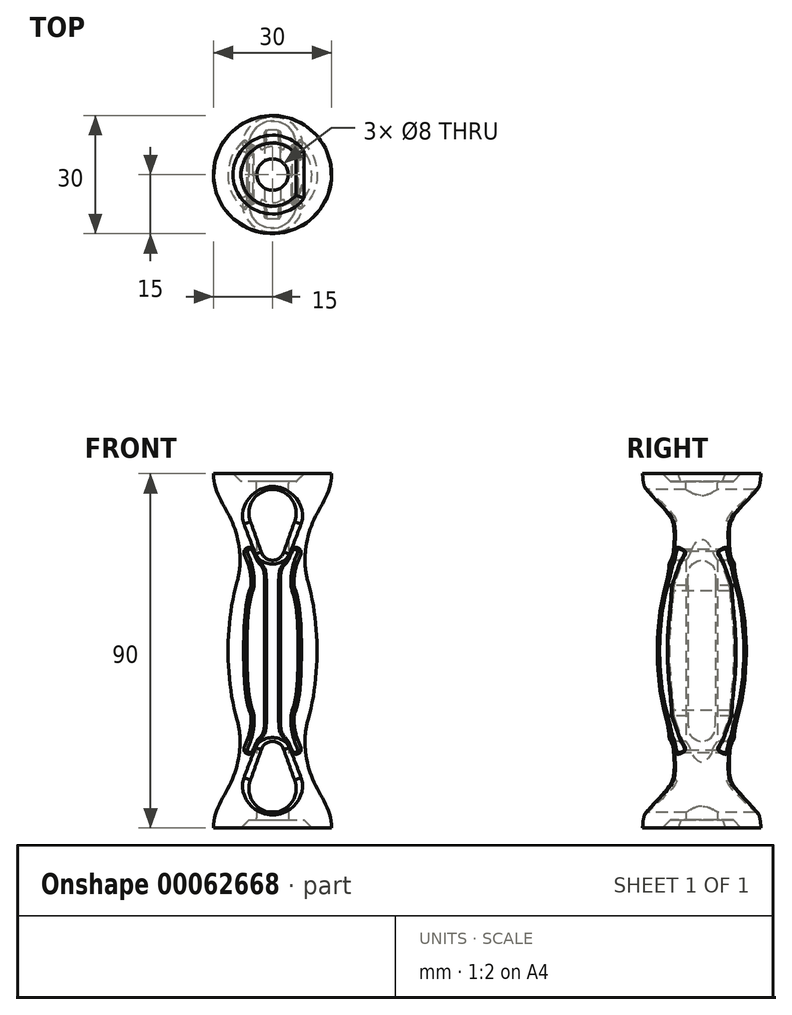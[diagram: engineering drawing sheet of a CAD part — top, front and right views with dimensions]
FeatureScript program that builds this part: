
annotation { "Feature Type Name" : "Feature", "Feature Type Description" : "" }
export const myFeature = defineFeature(function(context is Context, id is Id, definition is map)
    precondition{}
    {
        {
            var Q0;
            Q0=qCreatedBy(makeId("Front.planeOp"),FACE);
            var sketch = newSketch(context, id + "F0", { "sketchPlane" : qUnion([Q0])});
            skLineSegment(sketch, "E0", {"start": v(0, 0) * mm, "end": v(0, 45) * mm});
            skLineSegment(sketch, "E1", {"start": v(0, 45) * mm, "end": v(-15, 45) * mm});
            skLineSegment(sketch, "E2", {"start": v(0, 0) * mm, "end": v(-8, 0) * mm});
            skFitSpline(sketch, "E3", {"points": [v(-15, 45) * mm, v(-9.89, 31.85) * mm, v(-7.97, 5.04) * mm], "startDerivative": vector(-0.53, -36.4) * mm, "endDerivative": vector(-0.2, -58.1) * mm});
            skLineSegment(sketch, "E4.MirrorCS", {"start": v(0, -45) * mm, "end": v(-15, -45) * mm});
            skLineSegment(sketch, "E5.MirrorCS", {"start": v(0, 0) * mm, "end": v(0, -45) * mm});
            skFitSpline(sketch, "E6.MirrorCS", {"points": [v(-15, -45) * mm, v(-9.89, -31.85) * mm, v(-7.97, -5.04) * mm], "startDerivative": vector(-0.53, 36.4) * mm, "endDerivative": vector(-0.2, 58.1) * mm});
            skEllipticalArc(sketch, "E7", {});
            skPoint(sketch, "E8.MirrorCS.start.orphan", {"position": v(-8, 0) * mm});
            skPoint(sketch, "E9.visualSharp", {"position": v(-8, 20.72) * mm});
            skArc(sketch, "E9.filletArc", {"start": v(-9, 17.6) * mm, "mid": v(-8.3, 21.6) * mm, "end": v(-8.41, 25.67) * mm});
            skPoint(sketch, "E10.visualSharp", {"position": v(-8, -20.72) * mm});
            skArc(sketch, "E10.filletArc", {"start": v(-8.41, -25.67) * mm, "mid": v(-8.3, -21.6) * mm, "end": v(-9, -17.6) * mm});
            const initialGuessF0  = {"E7": [0.0066548618488013744, 0, 0, 1, 0.03582403436303139, 0.017969114314154242, 1.0572183333888945, 2.0843743202008995]};
            skSetInitialGuess(sketch, initialGuessF0);
            skSolve(sketch);
        }
        {
            var Q0;
            Q0=qSketchRegion(id+"F0",true);
            var Q1;
            Q1=sQuery(id+"F0.wireOp",EDGE,"E5.MirrorCS");
            revolve(context, id + "F1", {"entities" : qUnion([Q0]), "axis" : qUnion([Q1]), "revolveType" : RevolveType.FULL});
        }
        {
            var Q0;
            Q0=makeQuery(id+"F1.opRevolve","SWEPT_FACE",FACE,{"disambiguationData":[OSD([sQuery(id+"F0.wireOp",EDGE,"E4.MirrorCS")])]});
            var sketch = newSketch(context, id + "F2", { "sketchPlane" : qUnion([Q0])});
            skCircle(sketch, "E11", {"center": v(0, 0) * mm, "radius": 4 * mm});
            skSolve(sketch);
        }
        {
            var Q0;
            Q0=qSketchRegion(id+"F2",true);
            extrude(context, id + "F3", {"entities" : qUnion([Q0]), "operationType" : NewBodyOperationType.REMOVE, "oppositeDirection" : true, "depth" : 10 * mm});
        }
        {
            var Q0;
            Q0=qCreatedBy(makeId("Front.planeOp"),FACE);
            var sketch = newSketch(context, id + "F4", { "sketchPlane" : qUnion([Q0])});
            skLineSegment(sketch, "E12", {"start": v(0, 0) * mm, "end": v(0, 35) * mm});
            skArc(sketch, "E13", {"start": v(5.66, 33) * mm, "mid": v(0, 41) * mm, "end": v(-5.66, 33) * mm});
            skArc(sketch, "E14", {"start": v(-2.83, 25) * mm, "mid": v(0, 23) * mm, "end": v(2.83, 25) * mm});
            skLineSegment(sketch, "E15", {"start": v(5.66, 33) * mm, "end": v(2.83, 25) * mm});
            skLineSegment(sketch, "E16", {"start": v(-2.83, 25) * mm, "end": v(-5.66, 33) * mm});
            skLineSegment(sketch, "E17.MirrorCS", {"start": v(5.66, -33) * mm, "end": v(2.83, -25) * mm});
            skLineSegment(sketch, "E18.MirrorCS", {"start": v(0, 0) * mm, "end": v(0, -35) * mm});
            skLineSegment(sketch, "E19.MirrorCS", {"start": v(-2.83, -25) * mm, "end": v(-5.66, -33) * mm});
            skArc(sketch, "E20.MirrorCS", {"start": v(5.66, -33) * mm, "mid": v(0, -41) * mm, "end": v(-5.66, -33) * mm});
            skArc(sketch, "E21.MirrorCS", {"start": v(-2.83, -25) * mm, "mid": v(0, -23) * mm, "end": v(2.83, -25) * mm});
            skLineSegment(sketch, "E22", {"start": v(2, 16.6) * mm, "end": v(2, -16.6) * mm});
            skPoint(sketch, "E22.startSnap0", {"position": v(0, 17.5) * mm});
            skPoint(sketch, "E22.endSnap0", {"position": v(0, -17.5) * mm});
            skFitSpline(sketch, "E23", {"points": [v(2, 18) * mm, v(6.5, 0) * mm, v(2, -18) * mm], "startDerivative": vector(24, 0) * mm, "endDerivative": vector(-24, 0) * mm});
            skLineSegment(sketch, "E24.MirrorCS", {"start": v(-2, -16.6) * mm, "end": v(-2, -16.6) * mm});
            skPoint(sketch, "E25.MirrorP", {"position": v(-2, 18) * mm});
            skLineSegment(sketch, "E26.MirrorCS", {"start": v(-2, 16.6) * mm, "end": v(-2, -16.6) * mm});
            skFitSpline(sketch, "E27.MirrorCS", {"points": [v(-2, 18) * mm, v(-6.5, 0) * mm, v(-2, -18) * mm], "startDerivative": vector(-24, 0) * mm, "endDerivative": vector(24, 0) * mm});
            skFitSpline(sketch, "E28", {"points": [v(6.31, 25.3) * mm, v(6.31, 24.87) * mm, v(5.43, 22.53) * mm, v(4.64, 17.15) * mm, v(5.01, 15.16) * mm], "startDerivative": vector(0.28, -3.35) * mm, "endDerivative": vector(2.24, -7.03) * mm});
            skFitSpline(sketch, "E29", {"points": [v(6.31, 25.3) * mm, v(6.08, 25.65) * mm, v(5.45, 25.79) * mm, v(3.9, 22.88) * mm, v(2.45, 20.92) * mm, v(2, 16.6) * mm], "startDerivative": vector(-1.1, 4.8) * mm, "endDerivative": vector(0.4, -12.77) * mm});
            skPoint(sketch, "E30.filletArc.start.orphan", {"position": v(3.67, 17.34) * mm});
            skFitSpline(sketch, "E31.MirrorCS", {"points": [v(-6.31, 25.3) * mm, v(-6.31, 24.87) * mm, v(-5.43, 22.53) * mm, v(-4.64, 17.15) * mm, v(-5.01, 15.16) * mm], "startDerivative": vector(-0.28, -3.35) * mm, "endDerivative": vector(-2.24, -7.03) * mm});
            skFitSpline(sketch, "E32.MirrorCS", {"points": [v(-6.31, 25.3) * mm, v(-6.08, 25.65) * mm, v(-5.45, 25.79) * mm, v(-3.9, 22.88) * mm, v(-2.45, 20.92) * mm, v(-2, 16.6) * mm], "startDerivative": vector(1.1, 4.8) * mm, "endDerivative": vector(-0.4, -12.77) * mm});
            skPoint(sketch, "E33.MirrorCS.start.orphan", {"position": v(-3.67, 17.34) * mm});
            skLineSegment(sketch, "E34", {"start": v(0, 0) * mm, "end": v(-2, 0) * mm});
            skPoint(sketch, "E34.endSnap0", {"position": v(-2, 0) * mm});
            skFitSpline(sketch, "E35.MirrorCS", {"points": [v(6.31, -25.3) * mm, v(6.31, -24.87) * mm, v(5.43, -22.53) * mm, v(4.64, -17.15) * mm, v(5.01, -15.16) * mm], "startDerivative": vector(0.28, 3.35) * mm, "endDerivative": vector(2.24, 7.03) * mm});
            skFitSpline(sketch, "E36.MirrorCS", {"points": [v(6.31, -25.3) * mm, v(6.08, -25.65) * mm, v(5.45, -25.79) * mm, v(3.9, -22.88) * mm, v(2.45, -20.92) * mm, v(2, -16.6) * mm], "startDerivative": vector(-1.1, -4.8) * mm, "endDerivative": vector(0.4, 12.77) * mm});
            skFitSpline(sketch, "E37.MirrorCS", {"points": [v(-6.31, -25.3) * mm, v(-6.08, -25.65) * mm, v(-5.45, -25.79) * mm, v(-3.9, -22.88) * mm, v(-2.45, -20.92) * mm, v(-2, -16.6) * mm], "startDerivative": vector(1.1, -4.8) * mm, "endDerivative": vector(-0.4, 12.77) * mm});
            skFitSpline(sketch, "E38.MirrorCS", {"points": [v(-6.31, -25.3) * mm, v(-6.31, -24.87) * mm, v(-5.43, -22.53) * mm, v(-4.64, -17.15) * mm, v(-5.01, -15.16) * mm], "startDerivative": vector(-0.28, 3.35) * mm, "endDerivative": vector(-2.24, 7.03) * mm});
            skPoint(sketch, "E39.orphan", {"position": v(-3.67, -17.34) * mm});
            skPoint(sketch, "E40.filletArc.end.orphan", {"position": v(3.67, -17.34) * mm});
            skSolve(sketch);
        }
        {
            var Q0;
            Q0=qSketchRegion(id+"F4",true);
            extrude(context, id + "F5", {"entities" : qUnion([Q0]), "operationType" : NewBodyOperationType.REMOVE, "endBound" : BoundingType.THROUGH_ALL, "oppositeDirection" : true, "depth" : 25 * mm, "hasSecondDirection" : true, "secondDirectionOppositeDirection" : false, "secondDirectionDepth" : 25 * mm});
        }
        {
            var Q0;
            Q0=makeQuery(id+"F1.opRevolve","SWEPT_FACE",FACE,{"disambiguationData":[OSD([sQuery(id+"F0.wireOp",EDGE,"E1")])]});
            var sketch = newSketch(context, id + "F6", { "sketchPlane" : qUnion([Q0])});
            skCircle(sketch, "E41", {"center": v(0, 0) * mm, "radius": 4 * mm});
            skSolve(sketch);
        }
        {
            var Q0;
            Q0=qSketchRegion(id+"F6",true);
            extrude(context, id + "F7", {"entities" : qUnion([Q0]), "operationType" : NewBodyOperationType.REMOVE, "oppositeDirection" : true, "depth" : 10 * mm});
        }
        {
            var Q0;
            Q0=makeQuery(id+"F1.opRevolve","SWEPT_FACE",FACE,{"disambiguationData":[OSD([sQuery(id+"F0.wireOp",EDGE,"E4.MirrorCS")])]});
            var sketch = newSketch(context, id + "F8", { "sketchPlane" : qUnion([Q0])});
            skArc(sketch, "E42", {"start": v(-8, -6) * mm, "mid": v(10, 0) * mm, "end": v(-8, 6) * mm});
            skLineSegment(sketch, "E43", {"start": v(-8, -6) * mm, "end": v(-8, 6) * mm});
            skSolve(sketch);
        }
        {
            var Q0;
            Q0=qSketchRegion(id+"F8",true);
            extrude(context, id + "F9", {"entities" : qUnion([Q0]), "operationType" : NewBodyOperationType.REMOVE, "oppositeDirection" : true, "depth" : 2 * mm, "hasDraft" : true, "draftAngle" : 45 * degree, "draftPullDirection" : true});
        }
        {
            var Q0;
            Q0=makeQuery(id+"F1.opRevolve","SWEPT_FACE",FACE,{"disambiguationData":[OSD([sQuery(id+"F0.wireOp",EDGE,"E1")])]});
            var sketch = newSketch(context, id + "F10", { "sketchPlane" : qUnion([Q0])});
            skArc(sketch, "E44", {"start": v(8, 6) * mm, "mid": v(-10, 0) * mm, "end": v(8, -6) * mm});
            skLineSegment(sketch, "E45", {"start": v(8, 6) * mm, "end": v(8, -6) * mm});
            skSolve(sketch);
        }
        {
            var Q0;
            Q0=qSketchRegion(id+"F10",true);
            extrude(context, id + "F11", {"entities" : qUnion([Q0]), "operationType" : NewBodyOperationType.REMOVE, "oppositeDirection" : true, "depth" : 2 * mm, "hasDraft" : true, "draftAngle" : 45 * degree, "draftPullDirection" : true});
        }
        {
            var Q0;
            Q0=makeQuery(id+"F9.boolean.opBoolean","COPY",EDGE,{"derivedFrom":makeQuery(id+"F9.opExtrude","CAP_EDGE",EDGE,{"disambiguationData":[OSD([sQuery(id+"F8.wireOp",EDGE,"E42")])],"isStart":true})});
            var Q1;
            Q1=makeQuery(id+"F9.boolean.opBoolean","INTERSECT",EDGE,{"derivedFrom":[makeQuery(id+"F3.boolean.opBoolean","COPY",FACE,{"derivedFrom":makeQuery(id+"F3.opExtrude","SWEPT_FACE",FACE,{"disambiguationData":[OSD([sQuery(id+"F2.wireOp",EDGE,"E11")])]})}),makeQuery(id+"F9.opExtrude","CAP_FACE",FACE,{"disambiguationData":[OSD([sQuery(id+"F8.wireOp",EDGE,"E42")])],"isStart":false})]});
            var Q2;
            Q2=makeQuery(id+"F11.boolean.opBoolean","COPY",EDGE,{"derivedFrom":makeQuery(id+"F11.opExtrude","CAP_EDGE",EDGE,{"disambiguationData":[OSD([sQuery(id+"F10.wireOp",EDGE,"E44")])],"isStart":true})});
            var Q3;
            Q3=makeQuery(id+"F11.boolean.opBoolean","INTERSECT",EDGE,{"derivedFrom":[makeQuery(id+"F7.boolean.opBoolean","COPY",FACE,{"derivedFrom":makeQuery(id+"F7.opExtrude","SWEPT_FACE",FACE,{"disambiguationData":[OSD([sQuery(id+"F6.wireOp",EDGE,"E41")])]})}),makeQuery(id+"F11.opExtrude","CAP_FACE",FACE,{"disambiguationData":[OSD([sQuery(id+"F10.wireOp",EDGE,"E44")])],"isStart":false})]});
            var Q4;
            Q4=makeQuery(id+"F11.boolean.opBoolean","COPY",EDGE,{"derivedFrom":makeQuery(id+"F11.opExtrude","CAP_EDGE",EDGE,{"disambiguationData":[OSD([sQuery(id+"F10.wireOp",EDGE,"E45")])],"isStart":true})});
            var Q5;
            Q5=makeQuery(id+"F9.boolean.opBoolean","COPY",EDGE,{"derivedFrom":makeQuery(id+"F9.opExtrude","CAP_EDGE",EDGE,{"disambiguationData":[OSD([sQuery(id+"F8.wireOp",EDGE,"E43")])],"isStart":true})});
            fillet(context, id + "F12", {"entities" : qUnion([Q0, Q1, Q2, Q3, Q4, Q5]), "radius" : .5 * mm, "tangentPropagation" : true, "allowEdgeOverflow" : false});
        }
        {
            var Q0;
            Q0=makeQuery(id+"F9.boolean.opBoolean","COPY",FACE,{"derivedFrom":makeQuery(id+"F9.opExtrude","CAP_FACE",FACE,{"disambiguationData":[OSD([sQuery(id+"F8.wireOp",EDGE,"E42")])],"isStart":false})});
            var sketch = newSketch(context, id + "F13", { "sketchPlane" : qUnion([Q0])});
            skCircle(sketch, "E46", {"center": v(0, 0) * mm, "radius": 4 * mm});
            skSolve(sketch);
        }
        {
            var Q0;
            Q0=qSketchRegion(id+"F13",true);
            extrude(context, id + "F14", {"entities" : qUnion([Q0]), "operationType" : NewBodyOperationType.REMOVE, "endBound" : BoundingType.THROUGH_ALL, "oppositeDirection" : true, "depth" : 25 * mm});
        }
        {
            var Q0;
            Q0=makeQuery(id+"F5.boolean.opBoolean","INTERSECT",EDGE,{"disambiguationData":[OD(0.0)],"derivedFrom":[makeQuery(id+"F1.opRevolve","SWEPT_FACE",FACE,{"disambiguationData":[OSD([sQuery(id+"F0.wireOp",EDGE,"E6.MirrorCS")])]}),makeQuery(id+"F5.opExtrude","SWEPT_FACE",FACE,{"disambiguationData":[OSD([sQuery(id+"F4.wireOp",EDGE,"E20.MirrorCS")])]})]});
            var Q1;
            Q1=makeQuery(id+"F5.boolean.opBoolean","INTERSECT",EDGE,{"disambiguationData":[OD(0.0)],"derivedFrom":[makeQuery(id+"F1.opRevolve","SWEPT_FACE",FACE,{"disambiguationData":[OSD([sQuery(id+"F0.wireOp",EDGE,"E6.MirrorCS")])]}),makeQuery(id+"F5.opExtrude","SWEPT_FACE",FACE,{"disambiguationData":[OSD([sQuery(id+"F4.wireOp",EDGE,"E19.MirrorCS")])]})]});
            var Q2;
            Q2=makeQuery(id+"F5.boolean.opBoolean","INTERSECT",EDGE,{"disambiguationData":[OD(1.0)],"derivedFrom":[makeQuery(id+"F1.opRevolve","SWEPT_FACE",FACE,{"disambiguationData":[OSD([sQuery(id+"F0.wireOp",EDGE,"E6.MirrorCS")])]}),makeQuery(id+"F5.opExtrude","SWEPT_FACE",FACE,{"disambiguationData":[OSD([sQuery(id+"F4.wireOp",EDGE,"E20.MirrorCS")])]})]});
            var Q3;
            Q3=makeQuery(id+"F5.boolean.opBoolean","INTERSECT",EDGE,{"disambiguationData":[OD(0.0)],"derivedFrom":[makeQuery(id+"F1.opRevolve","SWEPT_FACE",FACE,{"disambiguationData":[OSD([sQuery(id+"F0.wireOp",EDGE,"E6.MirrorCS")])]}),makeQuery(id+"F5.opExtrude","SWEPT_FACE",FACE,{"disambiguationData":[OSD([sQuery(id+"F4.wireOp",EDGE,"E17.MirrorCS")])]})]});
            var Q4;
            Q4=makeQuery(id+"F5.boolean.opBoolean","INTERSECT",EDGE,{"disambiguationData":[OD(0.0)],"derivedFrom":[makeQuery(id+"F1.opRevolve","SWEPT_FACE",FACE,{"disambiguationData":[OSD([sQuery(id+"F0.wireOp",EDGE,"E10.filletArc")])]}),makeQuery(id+"F5.opExtrude","SWEPT_FACE",FACE,{"disambiguationData":[OSD([sQuery(id+"F4.wireOp",EDGE,"E21.MirrorCS")])]})]});
            var Q5;
            Q5=makeQuery(id+"F5.boolean.opBoolean","INTERSECT",EDGE,{"disambiguationData":[OD(0.0)],"derivedFrom":[makeQuery(id+"F1.opRevolve","SWEPT_FACE",FACE,{"disambiguationData":[OSD([sQuery(id+"F0.wireOp",EDGE,"E10.filletArc")])]}),makeQuery(id+"F5.opExtrude","SWEPT_FACE",FACE,{"disambiguationData":[OSD([sQuery(id+"F4.wireOp",EDGE,"E19.MirrorCS")])]})]});
            var Q6;
            Q6=makeQuery(id+"F5.boolean.opBoolean","INTERSECT",EDGE,{"disambiguationData":[OD(0.0)],"derivedFrom":[makeQuery(id+"F1.opRevolve","SWEPT_FACE",FACE,{"disambiguationData":[OSD([sQuery(id+"F0.wireOp",EDGE,"E10.filletArc")])]}),makeQuery(id+"F5.opExtrude","SWEPT_FACE",FACE,{"disambiguationData":[OSD([sQuery(id+"F4.wireOp",EDGE,"E17.MirrorCS")])]})]});
            var Q7;
            Q7=makeQuery(id+"F5.boolean.opBoolean","INTERSECT",EDGE,{"disambiguationData":[OD(1.0)],"derivedFrom":[makeQuery(id+"F1.opRevolve","SWEPT_FACE",FACE,{"disambiguationData":[OSD([sQuery(id+"F0.wireOp",EDGE,"E6.MirrorCS")])]}),makeQuery(id+"F5.opExtrude","SWEPT_FACE",FACE,{"disambiguationData":[OSD([sQuery(id+"F4.wireOp",EDGE,"E17.MirrorCS")])]})]});
            var Q8;
            Q8=makeQuery(id+"F5.boolean.opBoolean","INTERSECT",EDGE,{"disambiguationData":[OD(1.0)],"derivedFrom":[makeQuery(id+"F1.opRevolve","SWEPT_FACE",FACE,{"disambiguationData":[OSD([sQuery(id+"F0.wireOp",EDGE,"E6.MirrorCS")])]}),makeQuery(id+"F5.opExtrude","SWEPT_FACE",FACE,{"disambiguationData":[OSD([sQuery(id+"F4.wireOp",EDGE,"E19.MirrorCS")])]})]});
            var Q9;
            Q9=makeQuery(id+"F5.boolean.opBoolean","INTERSECT",EDGE,{"disambiguationData":[OD(1.0)],"derivedFrom":[makeQuery(id+"F1.opRevolve","SWEPT_FACE",FACE,{"disambiguationData":[OSD([sQuery(id+"F0.wireOp",EDGE,"E10.filletArc")])]}),makeQuery(id+"F5.opExtrude","SWEPT_FACE",FACE,{"disambiguationData":[OSD([sQuery(id+"F4.wireOp",EDGE,"E21.MirrorCS")])]})]});
            var Q10;
            Q10=makeQuery(id+"F5.boolean.opBoolean","INTERSECT",EDGE,{"disambiguationData":[OD(1.0)],"derivedFrom":[makeQuery(id+"F1.opRevolve","SWEPT_FACE",FACE,{"disambiguationData":[OSD([sQuery(id+"F0.wireOp",EDGE,"E10.filletArc")])]}),makeQuery(id+"F5.opExtrude","SWEPT_FACE",FACE,{"disambiguationData":[OSD([sQuery(id+"F4.wireOp",EDGE,"E19.MirrorCS")])]})]});
            var Q11;
            Q11=makeQuery(id+"F5.boolean.opBoolean","INTERSECT",EDGE,{"disambiguationData":[OD(1.0)],"derivedFrom":[makeQuery(id+"F1.opRevolve","SWEPT_FACE",FACE,{"disambiguationData":[OSD([sQuery(id+"F0.wireOp",EDGE,"E10.filletArc")])]}),makeQuery(id+"F5.opExtrude","SWEPT_FACE",FACE,{"disambiguationData":[OSD([sQuery(id+"F4.wireOp",EDGE,"E17.MirrorCS")])]})]});
            var Q12;
            Q12=makeQuery(id+"F5.boolean.opBoolean","INTERSECT",EDGE,{"disambiguationData":[OD(0.0)],"derivedFrom":[makeQuery(id+"F1.opRevolve","SWEPT_FACE",FACE,{"disambiguationData":[OSD([sQuery(id+"F0.wireOp",EDGE,"E9.filletArc")])]}),makeQuery(id+"F5.opExtrude","SWEPT_FACE",FACE,{"disambiguationData":[OSD([sQuery(id+"F4.wireOp",EDGE,"E14")])]})]});
            var Q13;
            Q13=makeQuery(id+"F5.boolean.opBoolean","INTERSECT",EDGE,{"disambiguationData":[OD(0.0)],"derivedFrom":[makeQuery(id+"F1.opRevolve","SWEPT_FACE",FACE,{"disambiguationData":[OSD([sQuery(id+"F0.wireOp",EDGE,"E9.filletArc")])]}),makeQuery(id+"F5.opExtrude","SWEPT_FACE",FACE,{"disambiguationData":[OSD([sQuery(id+"F4.wireOp",EDGE,"E16")])]})]});
            var Q14;
            Q14=makeQuery(id+"F5.boolean.opBoolean","INTERSECT",EDGE,{"disambiguationData":[OD(0.0)],"derivedFrom":[makeQuery(id+"F1.opRevolve","SWEPT_FACE",FACE,{"disambiguationData":[OSD([sQuery(id+"F0.wireOp",EDGE,"E9.filletArc")])]}),makeQuery(id+"F5.opExtrude","SWEPT_FACE",FACE,{"disambiguationData":[OSD([sQuery(id+"F4.wireOp",EDGE,"E15")])]})]});
            var Q15;
            Q15=makeQuery(id+"F5.boolean.opBoolean","INTERSECT",EDGE,{"disambiguationData":[OD(0.0)],"derivedFrom":[makeQuery(id+"F1.opRevolve","SWEPT_FACE",FACE,{"disambiguationData":[OSD([sQuery(id+"F0.wireOp",EDGE,"E3")])]}),makeQuery(id+"F5.opExtrude","SWEPT_FACE",FACE,{"disambiguationData":[OSD([sQuery(id+"F4.wireOp",EDGE,"E15")])]})]});
            var Q16;
            Q16=makeQuery(id+"F5.boolean.opBoolean","INTERSECT",EDGE,{"disambiguationData":[OD(0.0)],"derivedFrom":[makeQuery(id+"F1.opRevolve","SWEPT_FACE",FACE,{"disambiguationData":[OSD([sQuery(id+"F0.wireOp",EDGE,"E3")])]}),makeQuery(id+"F5.opExtrude","SWEPT_FACE",FACE,{"disambiguationData":[OSD([sQuery(id+"F4.wireOp",EDGE,"E16")])]})]});
            var Q17;
            Q17=makeQuery(id+"F5.boolean.opBoolean","INTERSECT",EDGE,{"disambiguationData":[OD(0.0)],"derivedFrom":[makeQuery(id+"F1.opRevolve","SWEPT_FACE",FACE,{"disambiguationData":[OSD([sQuery(id+"F0.wireOp",EDGE,"E3")])]}),makeQuery(id+"F5.opExtrude","SWEPT_FACE",FACE,{"disambiguationData":[OSD([sQuery(id+"F4.wireOp",EDGE,"E13")])]})]});
            var Q18;
            Q18=makeQuery(id+"F5.boolean.opBoolean","INTERSECT",EDGE,{"disambiguationData":[OD(1.0)],"derivedFrom":[makeQuery(id+"F1.opRevolve","SWEPT_FACE",FACE,{"disambiguationData":[OSD([sQuery(id+"F0.wireOp",EDGE,"E3")])]}),makeQuery(id+"F5.opExtrude","SWEPT_FACE",FACE,{"disambiguationData":[OSD([sQuery(id+"F4.wireOp",EDGE,"E13")])]})]});
            var Q19;
            Q19=makeQuery(id+"F5.boolean.opBoolean","INTERSECT",EDGE,{"disambiguationData":[OD(1.0)],"derivedFrom":[makeQuery(id+"F1.opRevolve","SWEPT_FACE",FACE,{"disambiguationData":[OSD([sQuery(id+"F0.wireOp",EDGE,"E3")])]}),makeQuery(id+"F5.opExtrude","SWEPT_FACE",FACE,{"disambiguationData":[OSD([sQuery(id+"F4.wireOp",EDGE,"E15")])]})]});
            var Q20;
            Q20=makeQuery(id+"F5.boolean.opBoolean","INTERSECT",EDGE,{"disambiguationData":[OD(1.0)],"derivedFrom":[makeQuery(id+"F1.opRevolve","SWEPT_FACE",FACE,{"disambiguationData":[OSD([sQuery(id+"F0.wireOp",EDGE,"E3")])]}),makeQuery(id+"F5.opExtrude","SWEPT_FACE",FACE,{"disambiguationData":[OSD([sQuery(id+"F4.wireOp",EDGE,"E16")])]})]});
            var Q21;
            Q21=makeQuery(id+"F5.boolean.opBoolean","INTERSECT",EDGE,{"disambiguationData":[OD(1.0)],"derivedFrom":[makeQuery(id+"F1.opRevolve","SWEPT_FACE",FACE,{"disambiguationData":[OSD([sQuery(id+"F0.wireOp",EDGE,"E9.filletArc")])]}),makeQuery(id+"F5.opExtrude","SWEPT_FACE",FACE,{"disambiguationData":[OSD([sQuery(id+"F4.wireOp",EDGE,"E14")])]})]});
            var Q22;
            Q22=makeQuery(id+"F5.boolean.opBoolean","INTERSECT",EDGE,{"disambiguationData":[OD(1.0)],"derivedFrom":[makeQuery(id+"F1.opRevolve","SWEPT_FACE",FACE,{"disambiguationData":[OSD([sQuery(id+"F0.wireOp",EDGE,"E9.filletArc")])]}),makeQuery(id+"F5.opExtrude","SWEPT_FACE",FACE,{"disambiguationData":[OSD([sQuery(id+"F4.wireOp",EDGE,"E16")])]})]});
            var Q23;
            Q23=makeQuery(id+"F5.boolean.opBoolean","INTERSECT",EDGE,{"disambiguationData":[OD(1.0)],"derivedFrom":[makeQuery(id+"F1.opRevolve","SWEPT_FACE",FACE,{"disambiguationData":[OSD([sQuery(id+"F0.wireOp",EDGE,"E9.filletArc")])]}),makeQuery(id+"F5.opExtrude","SWEPT_FACE",FACE,{"disambiguationData":[OSD([sQuery(id+"F4.wireOp",EDGE,"E15")])]})]});
            fillet(context, id + "F15", {"entities" : qUnion([Q0, Q1, Q2, Q3, Q4, Q5, Q6, Q7, Q8, Q9, Q10, Q11, Q12, Q13, Q14, Q15, Q16, Q17, Q18, Q19, Q20, Q21, Q22, Q23]), "radius" : 1 * mm, "tangentPropagation" : true, "allowEdgeOverflow" : false});
        }
        {
            var Q0;
            Q0=makeQuery(id+"F5.boolean.opBoolean","INTERSECT",EDGE,{"disambiguationData":[OD(0.0)],"derivedFrom":[makeQuery(id+"F1.opRevolve","SWEPT_FACE",FACE,{"disambiguationData":[OSD([sQuery(id+"F0.wireOp",EDGE,"E7")])]}),makeQuery(id+"F5.opExtrude","SWEPT_FACE",FACE,{"disambiguationData":[OSD([sQuery(id+"F4.wireOp",EDGE,"E27.MirrorCS")])]})]});
            var Q1;
            Q1=makeQuery(id+"F5.boolean.opBoolean","INTERSECT",EDGE,{"disambiguationData":[OD(0.0)],"derivedFrom":[makeQuery(id+"F1.opRevolve","SWEPT_FACE",FACE,{"disambiguationData":[OSD([sQuery(id+"F0.wireOp",EDGE,"E10.filletArc")])]}),makeQuery(id+"F5.opExtrude","SWEPT_FACE",FACE,{"disambiguationData":[OSD([sQuery(id+"F4.wireOp",EDGE,"E38.MirrorCS")])]})]});
            var Q2;
            Q2=makeQuery(id+"F5.boolean.opBoolean","INTERSECT",EDGE,{"disambiguationData":[OD(0.0)],"derivedFrom":[makeQuery(id+"F1.opRevolve","SWEPT_FACE",FACE,{"disambiguationData":[OSD([sQuery(id+"F0.wireOp",EDGE,"E7")])]}),makeQuery(id+"F5.opExtrude","SWEPT_FACE",FACE,{"disambiguationData":[OSD([sQuery(id+"F4.wireOp",EDGE,"E38.MirrorCS")])]})]});
            var Q3;
            Q3=makeQuery(id+"F5.boolean.opBoolean","INTERSECT",EDGE,{"disambiguationData":[OD(0.0)],"derivedFrom":[makeQuery(id+"F1.opRevolve","SWEPT_FACE",FACE,{"disambiguationData":[OSD([sQuery(id+"F0.wireOp",EDGE,"E7")])]}),makeQuery(id+"F5.opExtrude","SWEPT_FACE",FACE,{"disambiguationData":[OSD([sQuery(id+"F4.wireOp",EDGE,"E26.MirrorCS")])]})]});
            var Q4;
            Q4=makeQuery(id+"F5.boolean.opBoolean","INTERSECT",EDGE,{"disambiguationData":[OD(0.0)],"derivedFrom":[makeQuery(id+"F1.opRevolve","SWEPT_FACE",FACE,{"disambiguationData":[OSD([sQuery(id+"F0.wireOp",EDGE,"E7")])]}),makeQuery(id+"F5.opExtrude","SWEPT_FACE",FACE,{"disambiguationData":[OSD([sQuery(id+"F4.wireOp",EDGE,"E37.MirrorCS")])]})]});
            var Q5;
            Q5=makeQuery(id+"F5.boolean.opBoolean","INTERSECT",EDGE,{"disambiguationData":[OD(2.0)],"derivedFrom":[makeQuery(id+"F1.opRevolve","SWEPT_FACE",FACE,{"disambiguationData":[OSD([sQuery(id+"F0.wireOp",EDGE,"E10.filletArc")])]}),makeQuery(id+"F5.opExtrude","SWEPT_FACE",FACE,{"disambiguationData":[OSD([sQuery(id+"F4.wireOp",EDGE,"E37.MirrorCS")])]})]});
            var Q6;
            Q6=makeQuery(id+"F5.boolean.opBoolean","INTERSECT",EDGE,{"disambiguationData":[OD(0.0)],"derivedFrom":[makeQuery(id+"F1.opRevolve","SWEPT_FACE",FACE,{"disambiguationData":[OSD([sQuery(id+"F0.wireOp",EDGE,"E10.filletArc")])]}),makeQuery(id+"F5.opExtrude","SWEPT_FACE",FACE,{"disambiguationData":[OSD([sQuery(id+"F4.wireOp",EDGE,"E37.MirrorCS")])]})]});
            var Q7;
            Q7=makeQuery(id+"F5.boolean.opBoolean","INTERSECT",EDGE,{"disambiguationData":[OD(0.0)],"derivedFrom":[makeQuery(id+"F1.opRevolve","SWEPT_FACE",FACE,{"disambiguationData":[OSD([sQuery(id+"F0.wireOp",EDGE,"E6.MirrorCS")])]}),makeQuery(id+"F5.opExtrude","SWEPT_FACE",FACE,{"disambiguationData":[OSD([sQuery(id+"F4.wireOp",EDGE,"E37.MirrorCS")])]})]});
            var Q8;
            Q8=makeQuery(id+"F5.boolean.opBoolean","INTERSECT",EDGE,{"disambiguationData":[OD(2.0)],"derivedFrom":[makeQuery(id+"F1.opRevolve","SWEPT_FACE",FACE,{"disambiguationData":[OSD([sQuery(id+"F0.wireOp",EDGE,"E9.filletArc")])]}),makeQuery(id+"F5.opExtrude","SWEPT_FACE",FACE,{"disambiguationData":[OSD([sQuery(id+"F4.wireOp",EDGE,"E32.MirrorCS")])]})]});
            var Q9;
            Q9=makeQuery(id+"F5.boolean.opBoolean","INTERSECT",EDGE,{"disambiguationData":[OD(0.0)],"derivedFrom":[makeQuery(id+"F1.opRevolve","SWEPT_FACE",FACE,{"disambiguationData":[OSD([sQuery(id+"F0.wireOp",EDGE,"E7")])]}),makeQuery(id+"F5.opExtrude","SWEPT_FACE",FACE,{"disambiguationData":[OSD([sQuery(id+"F4.wireOp",EDGE,"E32.MirrorCS")])]})]});
            var Q10;
            Q10=makeQuery(id+"F5.boolean.opBoolean","INTERSECT",EDGE,{"disambiguationData":[OD(0.0)],"derivedFrom":[makeQuery(id+"F1.opRevolve","SWEPT_FACE",FACE,{"disambiguationData":[OSD([sQuery(id+"F0.wireOp",EDGE,"E7")])]}),makeQuery(id+"F5.opExtrude","SWEPT_FACE",FACE,{"disambiguationData":[OSD([sQuery(id+"F4.wireOp",EDGE,"E31.MirrorCS")])]})]});
            var Q11;
            Q11=makeQuery(id+"F5.boolean.opBoolean","INTERSECT",EDGE,{"disambiguationData":[OD(0.0)],"derivedFrom":[makeQuery(id+"F1.opRevolve","SWEPT_FACE",FACE,{"disambiguationData":[OSD([sQuery(id+"F0.wireOp",EDGE,"E9.filletArc")])]}),makeQuery(id+"F5.opExtrude","SWEPT_FACE",FACE,{"disambiguationData":[OSD([sQuery(id+"F4.wireOp",EDGE,"E31.MirrorCS")])]})]});
            var Q12;
            Q12=makeQuery(id+"F5.boolean.opBoolean","INTERSECT",EDGE,{"disambiguationData":[OD(0.0)],"derivedFrom":[makeQuery(id+"F1.opRevolve","SWEPT_FACE",FACE,{"disambiguationData":[OSD([sQuery(id+"F0.wireOp",EDGE,"E3")])]}),makeQuery(id+"F5.opExtrude","SWEPT_FACE",FACE,{"disambiguationData":[OSD([sQuery(id+"F4.wireOp",EDGE,"E32.MirrorCS")])]})]});
            var Q13;
            Q13=makeQuery(id+"F5.boolean.opBoolean","INTERSECT",EDGE,{"disambiguationData":[OD(0.0)],"derivedFrom":[makeQuery(id+"F1.opRevolve","SWEPT_FACE",FACE,{"disambiguationData":[OSD([sQuery(id+"F0.wireOp",EDGE,"E9.filletArc")])]}),makeQuery(id+"F5.opExtrude","SWEPT_FACE",FACE,{"disambiguationData":[OSD([sQuery(id+"F4.wireOp",EDGE,"E32.MirrorCS")])]})]});
            var Q14;
            Q14=makeQuery(id+"F5.boolean.opBoolean","INTERSECT",EDGE,{"disambiguationData":[OD(0.0)],"derivedFrom":[makeQuery(id+"F1.opRevolve","SWEPT_FACE",FACE,{"disambiguationData":[OSD([sQuery(id+"F0.wireOp",EDGE,"E7")])]}),makeQuery(id+"F5.opExtrude","SWEPT_FACE",FACE,{"disambiguationData":[OSD([sQuery(id+"F4.wireOp",EDGE,"E22")])]})]});
            var Q15;
            Q15=makeQuery(id+"F5.boolean.opBoolean","INTERSECT",EDGE,{"disambiguationData":[OD(2.0)],"derivedFrom":[makeQuery(id+"F1.opRevolve","SWEPT_FACE",FACE,{"disambiguationData":[OSD([sQuery(id+"F0.wireOp",EDGE,"E9.filletArc")])]}),makeQuery(id+"F5.opExtrude","SWEPT_FACE",FACE,{"disambiguationData":[OSD([sQuery(id+"F4.wireOp",EDGE,"E29")])]})]});
            var Q16;
            Q16=makeQuery(id+"F5.boolean.opBoolean","INTERSECT",EDGE,{"disambiguationData":[OD(0.0)],"derivedFrom":[makeQuery(id+"F1.opRevolve","SWEPT_FACE",FACE,{"disambiguationData":[OSD([sQuery(id+"F0.wireOp",EDGE,"E7")])]}),makeQuery(id+"F5.opExtrude","SWEPT_FACE",FACE,{"disambiguationData":[OSD([sQuery(id+"F4.wireOp",EDGE,"E29")])]})]});
            var Q17;
            Q17=makeQuery(id+"F5.boolean.opBoolean","INTERSECT",EDGE,{"disambiguationData":[OD(0.0)],"derivedFrom":[makeQuery(id+"F1.opRevolve","SWEPT_FACE",FACE,{"disambiguationData":[OSD([sQuery(id+"F0.wireOp",EDGE,"E3")])]}),makeQuery(id+"F5.opExtrude","SWEPT_FACE",FACE,{"disambiguationData":[OSD([sQuery(id+"F4.wireOp",EDGE,"E29")])]})]});
            var Q18;
            Q18=makeQuery(id+"F5.boolean.opBoolean","INTERSECT",EDGE,{"disambiguationData":[OD(0.0)],"derivedFrom":[makeQuery(id+"F1.opRevolve","SWEPT_FACE",FACE,{"disambiguationData":[OSD([sQuery(id+"F0.wireOp",EDGE,"E9.filletArc")])]}),makeQuery(id+"F5.opExtrude","SWEPT_FACE",FACE,{"disambiguationData":[OSD([sQuery(id+"F4.wireOp",EDGE,"E29")])]})]});
            var Q19;
            Q19=makeQuery(id+"F5.boolean.opBoolean","INTERSECT",EDGE,{"disambiguationData":[OD(0.0)],"derivedFrom":[makeQuery(id+"F1.opRevolve","SWEPT_FACE",FACE,{"disambiguationData":[OSD([sQuery(id+"F0.wireOp",EDGE,"E9.filletArc")])]}),makeQuery(id+"F5.opExtrude","SWEPT_FACE",FACE,{"disambiguationData":[OSD([sQuery(id+"F4.wireOp",EDGE,"E28")])]})]});
            var Q20;
            Q20=makeQuery(id+"F5.boolean.opBoolean","INTERSECT",EDGE,{"disambiguationData":[OD(0.0)],"derivedFrom":[makeQuery(id+"F1.opRevolve","SWEPT_FACE",FACE,{"disambiguationData":[OSD([sQuery(id+"F0.wireOp",EDGE,"E7")])]}),makeQuery(id+"F5.opExtrude","SWEPT_FACE",FACE,{"disambiguationData":[OSD([sQuery(id+"F4.wireOp",EDGE,"E28")])]})]});
            var Q21;
            Q21=makeQuery(id+"F5.boolean.opBoolean","INTERSECT",EDGE,{"disambiguationData":[OD(0.0)],"derivedFrom":[makeQuery(id+"F1.opRevolve","SWEPT_FACE",FACE,{"disambiguationData":[OSD([sQuery(id+"F0.wireOp",EDGE,"E7")])]}),makeQuery(id+"F5.opExtrude","SWEPT_FACE",FACE,{"disambiguationData":[OSD([sQuery(id+"F4.wireOp",EDGE,"E23")])]})]});
            var Q22;
            Q22=makeQuery(id+"F5.boolean.opBoolean","INTERSECT",EDGE,{"disambiguationData":[OD(0.0)],"derivedFrom":[makeQuery(id+"F1.opRevolve","SWEPT_FACE",FACE,{"disambiguationData":[OSD([sQuery(id+"F0.wireOp",EDGE,"E7")])]}),makeQuery(id+"F5.opExtrude","SWEPT_FACE",FACE,{"disambiguationData":[OSD([sQuery(id+"F4.wireOp",EDGE,"E35.MirrorCS")])]})]});
            var Q23;
            Q23=makeQuery(id+"F5.boolean.opBoolean","INTERSECT",EDGE,{"disambiguationData":[OD(0.0)],"derivedFrom":[makeQuery(id+"F1.opRevolve","SWEPT_FACE",FACE,{"disambiguationData":[OSD([sQuery(id+"F0.wireOp",EDGE,"E10.filletArc")])]}),makeQuery(id+"F5.opExtrude","SWEPT_FACE",FACE,{"disambiguationData":[OSD([sQuery(id+"F4.wireOp",EDGE,"E35.MirrorCS")])]})]});
            var Q24;
            Q24=makeQuery(id+"F5.boolean.opBoolean","INTERSECT",EDGE,{"disambiguationData":[OD(0.0)],"derivedFrom":[makeQuery(id+"F1.opRevolve","SWEPT_FACE",FACE,{"disambiguationData":[OSD([sQuery(id+"F0.wireOp",EDGE,"E10.filletArc")])]}),makeQuery(id+"F5.opExtrude","SWEPT_FACE",FACE,{"disambiguationData":[OSD([sQuery(id+"F4.wireOp",EDGE,"E36.MirrorCS")])]})]});
            var Q25;
            Q25=makeQuery(id+"F5.boolean.opBoolean","INTERSECT",EDGE,{"disambiguationData":[OD(0.0)],"derivedFrom":[makeQuery(id+"F1.opRevolve","SWEPT_FACE",FACE,{"disambiguationData":[OSD([sQuery(id+"F0.wireOp",EDGE,"E6.MirrorCS")])]}),makeQuery(id+"F5.opExtrude","SWEPT_FACE",FACE,{"disambiguationData":[OSD([sQuery(id+"F4.wireOp",EDGE,"E36.MirrorCS")])]})]});
            var Q26;
            Q26=makeQuery(id+"F5.boolean.opBoolean","INTERSECT",EDGE,{"disambiguationData":[OD(2.0)],"derivedFrom":[makeQuery(id+"F1.opRevolve","SWEPT_FACE",FACE,{"disambiguationData":[OSD([sQuery(id+"F0.wireOp",EDGE,"E10.filletArc")])]}),makeQuery(id+"F5.opExtrude","SWEPT_FACE",FACE,{"disambiguationData":[OSD([sQuery(id+"F4.wireOp",EDGE,"E36.MirrorCS")])]})]});
            var Q27;
            Q27=makeQuery(id+"F5.boolean.opBoolean","INTERSECT",EDGE,{"disambiguationData":[OD(0.0)],"derivedFrom":[makeQuery(id+"F1.opRevolve","SWEPT_FACE",FACE,{"disambiguationData":[OSD([sQuery(id+"F0.wireOp",EDGE,"E7")])]}),makeQuery(id+"F5.opExtrude","SWEPT_FACE",FACE,{"disambiguationData":[OSD([sQuery(id+"F4.wireOp",EDGE,"E36.MirrorCS")])]})]});
            var Q28;
            Q28=makeQuery(id+"F5.boolean.opBoolean","INTERSECT",EDGE,{"disambiguationData":[OD(1.0)],"derivedFrom":[makeQuery(id+"F1.opRevolve","SWEPT_FACE",FACE,{"disambiguationData":[OSD([sQuery(id+"F0.wireOp",EDGE,"E10.filletArc")])]}),makeQuery(id+"F5.opExtrude","SWEPT_FACE",FACE,{"disambiguationData":[OSD([sQuery(id+"F4.wireOp",EDGE,"E38.MirrorCS")])]})]});
            var Q29;
            Q29=makeQuery(id+"F5.boolean.opBoolean","INTERSECT",EDGE,{"disambiguationData":[OD(1.0)],"derivedFrom":[makeQuery(id+"F1.opRevolve","SWEPT_FACE",FACE,{"disambiguationData":[OSD([sQuery(id+"F0.wireOp",EDGE,"E10.filletArc")])]}),makeQuery(id+"F5.opExtrude","SWEPT_FACE",FACE,{"disambiguationData":[OSD([sQuery(id+"F4.wireOp",EDGE,"E37.MirrorCS")])]})]});
            var Q30;
            Q30=makeQuery(id+"F5.boolean.opBoolean","INTERSECT",EDGE,{"disambiguationData":[OD(1.0)],"derivedFrom":[makeQuery(id+"F1.opRevolve","SWEPT_FACE",FACE,{"disambiguationData":[OSD([sQuery(id+"F0.wireOp",EDGE,"E6.MirrorCS")])]}),makeQuery(id+"F5.opExtrude","SWEPT_FACE",FACE,{"disambiguationData":[OSD([sQuery(id+"F4.wireOp",EDGE,"E37.MirrorCS")])]})]});
            var Q31;
            Q31=makeQuery(id+"F5.boolean.opBoolean","INTERSECT",EDGE,{"disambiguationData":[OD(3.0)],"derivedFrom":[makeQuery(id+"F1.opRevolve","SWEPT_FACE",FACE,{"disambiguationData":[OSD([sQuery(id+"F0.wireOp",EDGE,"E10.filletArc")])]}),makeQuery(id+"F5.opExtrude","SWEPT_FACE",FACE,{"disambiguationData":[OSD([sQuery(id+"F4.wireOp",EDGE,"E37.MirrorCS")])]})]});
            var Q32;
            Q32=makeQuery(id+"F5.boolean.opBoolean","INTERSECT",EDGE,{"disambiguationData":[OD(1.0)],"derivedFrom":[makeQuery(id+"F1.opRevolve","SWEPT_FACE",FACE,{"disambiguationData":[OSD([sQuery(id+"F0.wireOp",EDGE,"E7")])]}),makeQuery(id+"F5.opExtrude","SWEPT_FACE",FACE,{"disambiguationData":[OSD([sQuery(id+"F4.wireOp",EDGE,"E26.MirrorCS")])]})]});
            var Q33;
            Q33=makeQuery(id+"F5.boolean.opBoolean","INTERSECT",EDGE,{"disambiguationData":[OD(1.0)],"derivedFrom":[makeQuery(id+"F1.opRevolve","SWEPT_FACE",FACE,{"disambiguationData":[OSD([sQuery(id+"F0.wireOp",EDGE,"E7")])]}),makeQuery(id+"F5.opExtrude","SWEPT_FACE",FACE,{"disambiguationData":[OSD([sQuery(id+"F4.wireOp",EDGE,"E37.MirrorCS")])]})]});
            var Q34;
            Q34=makeQuery(id+"F5.boolean.opBoolean","INTERSECT",EDGE,{"disambiguationData":[OD(1.0)],"derivedFrom":[makeQuery(id+"F1.opRevolve","SWEPT_FACE",FACE,{"disambiguationData":[OSD([sQuery(id+"F0.wireOp",EDGE,"E7")])]}),makeQuery(id+"F5.opExtrude","SWEPT_FACE",FACE,{"disambiguationData":[OSD([sQuery(id+"F4.wireOp",EDGE,"E38.MirrorCS")])]})]});
            var Q35;
            Q35=makeQuery(id+"F5.boolean.opBoolean","INTERSECT",EDGE,{"disambiguationData":[OD(1.0)],"derivedFrom":[makeQuery(id+"F1.opRevolve","SWEPT_FACE",FACE,{"disambiguationData":[OSD([sQuery(id+"F0.wireOp",EDGE,"E7")])]}),makeQuery(id+"F5.opExtrude","SWEPT_FACE",FACE,{"disambiguationData":[OSD([sQuery(id+"F4.wireOp",EDGE,"E27.MirrorCS")])]})]});
            var Q36;
            Q36=makeQuery(id+"F5.boolean.opBoolean","INTERSECT",EDGE,{"disambiguationData":[OD(1.0)],"derivedFrom":[makeQuery(id+"F1.opRevolve","SWEPT_FACE",FACE,{"disambiguationData":[OSD([sQuery(id+"F0.wireOp",EDGE,"E7")])]}),makeQuery(id+"F5.opExtrude","SWEPT_FACE",FACE,{"disambiguationData":[OSD([sQuery(id+"F4.wireOp",EDGE,"E31.MirrorCS")])]})]});
            var Q37;
            Q37=makeQuery(id+"F5.boolean.opBoolean","INTERSECT",EDGE,{"disambiguationData":[OD(1.0)],"derivedFrom":[makeQuery(id+"F1.opRevolve","SWEPT_FACE",FACE,{"disambiguationData":[OSD([sQuery(id+"F0.wireOp",EDGE,"E7")])]}),makeQuery(id+"F5.opExtrude","SWEPT_FACE",FACE,{"disambiguationData":[OSD([sQuery(id+"F4.wireOp",EDGE,"E32.MirrorCS")])]})]});
            var Q38;
            Q38=makeQuery(id+"F5.boolean.opBoolean","INTERSECT",EDGE,{"disambiguationData":[OD(3.0)],"derivedFrom":[makeQuery(id+"F1.opRevolve","SWEPT_FACE",FACE,{"disambiguationData":[OSD([sQuery(id+"F0.wireOp",EDGE,"E9.filletArc")])]}),makeQuery(id+"F5.opExtrude","SWEPT_FACE",FACE,{"disambiguationData":[OSD([sQuery(id+"F4.wireOp",EDGE,"E32.MirrorCS")])]})]});
            var Q39;
            Q39=makeQuery(id+"F5.boolean.opBoolean","INTERSECT",EDGE,{"disambiguationData":[OD(1.0)],"derivedFrom":[makeQuery(id+"F1.opRevolve","SWEPT_FACE",FACE,{"disambiguationData":[OSD([sQuery(id+"F0.wireOp",EDGE,"E9.filletArc")])]}),makeQuery(id+"F5.opExtrude","SWEPT_FACE",FACE,{"disambiguationData":[OSD([sQuery(id+"F4.wireOp",EDGE,"E31.MirrorCS")])]})]});
            var Q40;
            Q40=makeQuery(id+"F5.boolean.opBoolean","INTERSECT",EDGE,{"disambiguationData":[OD(1.0)],"derivedFrom":[makeQuery(id+"F1.opRevolve","SWEPT_FACE",FACE,{"disambiguationData":[OSD([sQuery(id+"F0.wireOp",EDGE,"E3")])]}),makeQuery(id+"F5.opExtrude","SWEPT_FACE",FACE,{"disambiguationData":[OSD([sQuery(id+"F4.wireOp",EDGE,"E32.MirrorCS")])]})]});
            var Q41;
            Q41=makeQuery(id+"F5.boolean.opBoolean","INTERSECT",EDGE,{"disambiguationData":[OD(1.0)],"derivedFrom":[makeQuery(id+"F1.opRevolve","SWEPT_FACE",FACE,{"disambiguationData":[OSD([sQuery(id+"F0.wireOp",EDGE,"E9.filletArc")])]}),makeQuery(id+"F5.opExtrude","SWEPT_FACE",FACE,{"disambiguationData":[OSD([sQuery(id+"F4.wireOp",EDGE,"E32.MirrorCS")])]})]});
            var Q42;
            Q42=makeQuery(id+"F5.boolean.opBoolean","INTERSECT",EDGE,{"disambiguationData":[OD(3.0)],"derivedFrom":[makeQuery(id+"F1.opRevolve","SWEPT_FACE",FACE,{"disambiguationData":[OSD([sQuery(id+"F0.wireOp",EDGE,"E9.filletArc")])]}),makeQuery(id+"F5.opExtrude","SWEPT_FACE",FACE,{"disambiguationData":[OSD([sQuery(id+"F4.wireOp",EDGE,"E29")])]})]});
            var Q43;
            Q43=makeQuery(id+"F5.boolean.opBoolean","INTERSECT",EDGE,{"disambiguationData":[OD(1.0)],"derivedFrom":[makeQuery(id+"F1.opRevolve","SWEPT_FACE",FACE,{"disambiguationData":[OSD([sQuery(id+"F0.wireOp",EDGE,"E7")])]}),makeQuery(id+"F5.opExtrude","SWEPT_FACE",FACE,{"disambiguationData":[OSD([sQuery(id+"F4.wireOp",EDGE,"E29")])]})]});
            var Q44;
            Q44=makeQuery(id+"F5.boolean.opBoolean","INTERSECT",EDGE,{"disambiguationData":[OD(1.0)],"derivedFrom":[makeQuery(id+"F1.opRevolve","SWEPT_FACE",FACE,{"disambiguationData":[OSD([sQuery(id+"F0.wireOp",EDGE,"E7")])]}),makeQuery(id+"F5.opExtrude","SWEPT_FACE",FACE,{"disambiguationData":[OSD([sQuery(id+"F4.wireOp",EDGE,"E22")])]})]});
            var Q45;
            Q45=makeQuery(id+"F5.boolean.opBoolean","INTERSECT",EDGE,{"disambiguationData":[OD(1.0)],"derivedFrom":[makeQuery(id+"F1.opRevolve","SWEPT_FACE",FACE,{"disambiguationData":[OSD([sQuery(id+"F0.wireOp",EDGE,"E7")])]}),makeQuery(id+"F5.opExtrude","SWEPT_FACE",FACE,{"disambiguationData":[OSD([sQuery(id+"F4.wireOp",EDGE,"E36.MirrorCS")])]})]});
            var Q46;
            Q46=makeQuery(id+"F5.boolean.opBoolean","INTERSECT",EDGE,{"disambiguationData":[OD(3.0)],"derivedFrom":[makeQuery(id+"F1.opRevolve","SWEPT_FACE",FACE,{"disambiguationData":[OSD([sQuery(id+"F0.wireOp",EDGE,"E10.filletArc")])]}),makeQuery(id+"F5.opExtrude","SWEPT_FACE",FACE,{"disambiguationData":[OSD([sQuery(id+"F4.wireOp",EDGE,"E36.MirrorCS")])]})]});
            var Q47;
            Q47=makeQuery(id+"F5.boolean.opBoolean","INTERSECT",EDGE,{"disambiguationData":[OD(1.0)],"derivedFrom":[makeQuery(id+"F1.opRevolve","SWEPT_FACE",FACE,{"disambiguationData":[OSD([sQuery(id+"F0.wireOp",EDGE,"E6.MirrorCS")])]}),makeQuery(id+"F5.opExtrude","SWEPT_FACE",FACE,{"disambiguationData":[OSD([sQuery(id+"F4.wireOp",EDGE,"E36.MirrorCS")])]})]});
            var Q48;
            Q48=makeQuery(id+"F5.boolean.opBoolean","INTERSECT",EDGE,{"disambiguationData":[OD(1.0)],"derivedFrom":[makeQuery(id+"F1.opRevolve","SWEPT_FACE",FACE,{"disambiguationData":[OSD([sQuery(id+"F0.wireOp",EDGE,"E10.filletArc")])]}),makeQuery(id+"F5.opExtrude","SWEPT_FACE",FACE,{"disambiguationData":[OSD([sQuery(id+"F4.wireOp",EDGE,"E36.MirrorCS")])]})]});
            var Q49;
            Q49=makeQuery(id+"F5.boolean.opBoolean","INTERSECT",EDGE,{"disambiguationData":[OD(1.0)],"derivedFrom":[makeQuery(id+"F1.opRevolve","SWEPT_FACE",FACE,{"disambiguationData":[OSD([sQuery(id+"F0.wireOp",EDGE,"E10.filletArc")])]}),makeQuery(id+"F5.opExtrude","SWEPT_FACE",FACE,{"disambiguationData":[OSD([sQuery(id+"F4.wireOp",EDGE,"E35.MirrorCS")])]})]});
            var Q50;
            Q50=makeQuery(id+"F5.boolean.opBoolean","INTERSECT",EDGE,{"disambiguationData":[OD(1.0)],"derivedFrom":[makeQuery(id+"F1.opRevolve","SWEPT_FACE",FACE,{"disambiguationData":[OSD([sQuery(id+"F0.wireOp",EDGE,"E7")])]}),makeQuery(id+"F5.opExtrude","SWEPT_FACE",FACE,{"disambiguationData":[OSD([sQuery(id+"F4.wireOp",EDGE,"E35.MirrorCS")])]})]});
            var Q51;
            Q51=makeQuery(id+"F5.boolean.opBoolean","INTERSECT",EDGE,{"disambiguationData":[OD(1.0)],"derivedFrom":[makeQuery(id+"F1.opRevolve","SWEPT_FACE",FACE,{"disambiguationData":[OSD([sQuery(id+"F0.wireOp",EDGE,"E7")])]}),makeQuery(id+"F5.opExtrude","SWEPT_FACE",FACE,{"disambiguationData":[OSD([sQuery(id+"F4.wireOp",EDGE,"E23")])]})]});
            var Q52;
            Q52=makeQuery(id+"F5.boolean.opBoolean","INTERSECT",EDGE,{"disambiguationData":[OD(1.0)],"derivedFrom":[makeQuery(id+"F1.opRevolve","SWEPT_FACE",FACE,{"disambiguationData":[OSD([sQuery(id+"F0.wireOp",EDGE,"E7")])]}),makeQuery(id+"F5.opExtrude","SWEPT_FACE",FACE,{"disambiguationData":[OSD([sQuery(id+"F4.wireOp",EDGE,"E28")])]})]});
            var Q53;
            Q53=makeQuery(id+"F5.boolean.opBoolean","INTERSECT",EDGE,{"disambiguationData":[OD(1.0)],"derivedFrom":[makeQuery(id+"F1.opRevolve","SWEPT_FACE",FACE,{"disambiguationData":[OSD([sQuery(id+"F0.wireOp",EDGE,"E9.filletArc")])]}),makeQuery(id+"F5.opExtrude","SWEPT_FACE",FACE,{"disambiguationData":[OSD([sQuery(id+"F4.wireOp",EDGE,"E28")])]})]});
            var Q54;
            Q54=makeQuery(id+"F5.boolean.opBoolean","INTERSECT",EDGE,{"disambiguationData":[OD(1.0)],"derivedFrom":[makeQuery(id+"F1.opRevolve","SWEPT_FACE",FACE,{"disambiguationData":[OSD([sQuery(id+"F0.wireOp",EDGE,"E3")])]}),makeQuery(id+"F5.opExtrude","SWEPT_FACE",FACE,{"disambiguationData":[OSD([sQuery(id+"F4.wireOp",EDGE,"E29")])]})]});
            var Q55;
            Q55=makeQuery(id+"F5.boolean.opBoolean","INTERSECT",EDGE,{"disambiguationData":[OD(1.0)],"derivedFrom":[makeQuery(id+"F1.opRevolve","SWEPT_FACE",FACE,{"disambiguationData":[OSD([sQuery(id+"F0.wireOp",EDGE,"E9.filletArc")])]}),makeQuery(id+"F5.opExtrude","SWEPT_FACE",FACE,{"disambiguationData":[OSD([sQuery(id+"F4.wireOp",EDGE,"E29")])]})]});
            fillet(context, id + "F16", {"entities" : qUnion([Q0, Q1, Q2, Q3, Q4, Q5, Q6, Q7, Q8, Q9, Q10, Q11, Q12, Q13, Q14, Q15, Q16, Q17, Q18, Q19, Q20, Q21, Q22, Q23, Q24, Q25, Q26, Q27, Q28, Q29, Q30, Q31, Q32, Q33, Q34, Q35, Q36, Q37, Q38, Q39, Q40, Q41, Q42, Q43, Q44, Q45, Q46, Q47, Q48, Q49, Q50, Q51, Q52, Q53, Q54, Q55]), "radius" : .5 * mm, "tangentPropagation" : true, "allowEdgeOverflow" : false});
        }
    });
